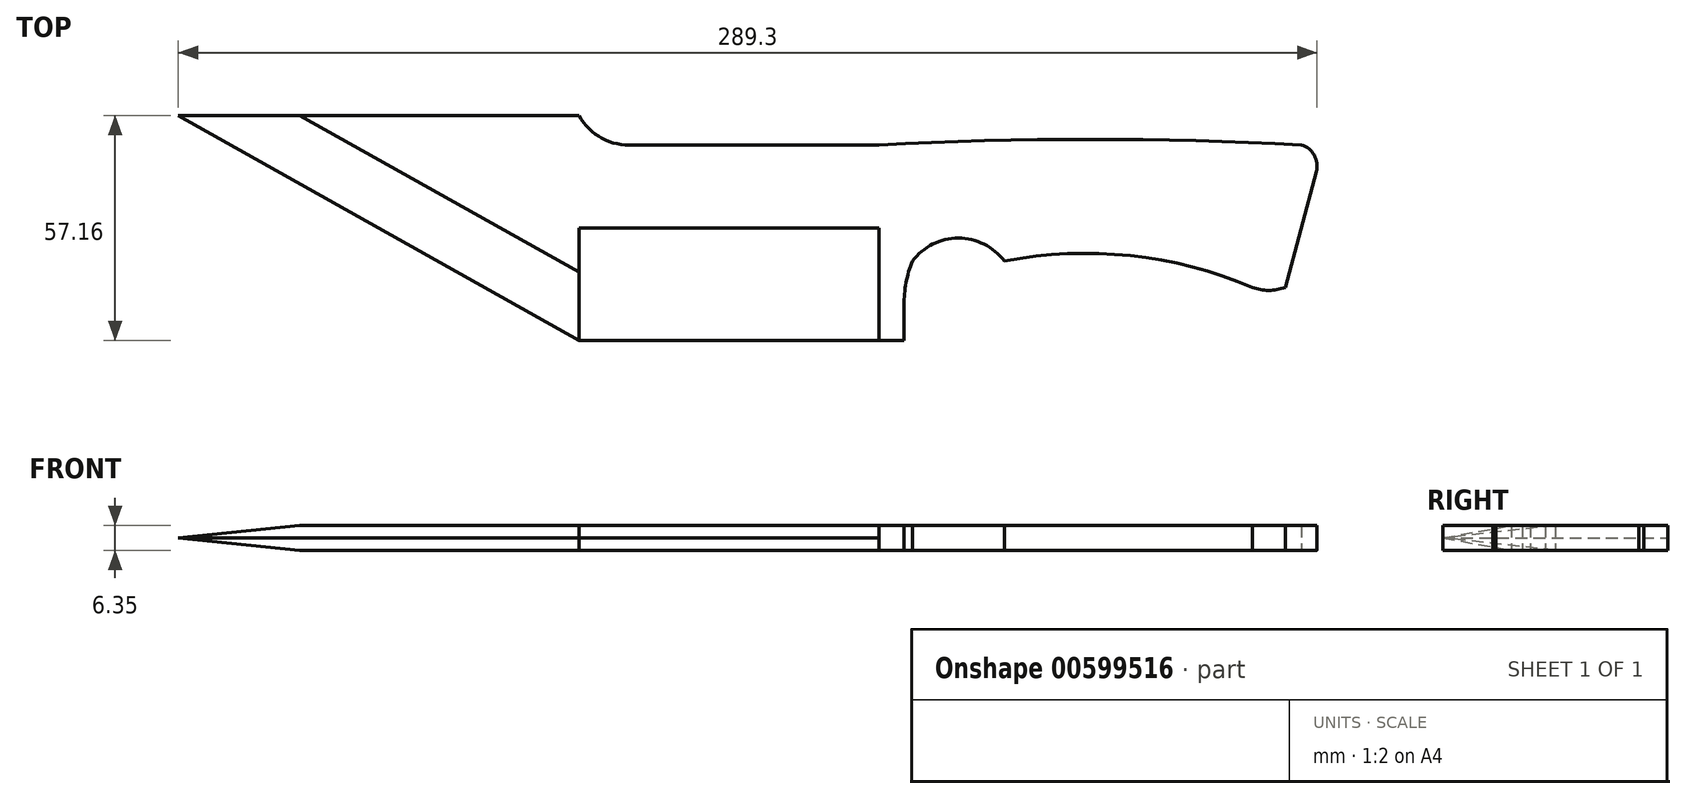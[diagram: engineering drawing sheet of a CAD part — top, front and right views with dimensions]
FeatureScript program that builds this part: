
annotation { "Feature Type Name" : "Feature", "Feature Type Description" : "" }
export const myFeature = defineFeature(function(context is Context, id is Id, definition is map)
    precondition{}
    {
        {
            var Q0;
            Q0=qCreatedBy(makeId("Top.planeOp"),FACE);
            var sketch = newSketch(context, id + "F0", { "sketchPlane" : qUnion([Q0])});
            skPoint(sketch, "E0.middle", {"position": v(0, 0) * mm});
            skLineSegment(sketch, "E1", {"start": v(-44.2, -28.58) * mm, "end": v(-146.05, 28.58) * mm});
            skLineSegment(sketch, "E2", {"start": v(-44.2, -28.58) * mm, "end": v(31.94, -28.58) * mm});
            skLineSegment(sketch, "E3", {"start": v(31.94, -28.58) * mm, "end": v(38.32, -28.58) * mm});
            skArc(sketch, "E4", {"start": v(-44.2, 28.58) * mm, "mid": v(-38.45, 22.79) * mm, "end": v(-30.46, 21.12) * mm});
            skLineSegment(sketch, "E5", {"start": v(-30.46, 21.12) * mm, "end": v(31.94, 21.12) * mm});
            skLineSegment(sketch, "E6", {"start": v(-146.05, 28.58) * mm, "end": v(-44.2, 28.58) * mm});
            skLineSegment(sketch, "E7", {"start": v(38.32, -28.58) * mm, "end": v(38.32, -19.6) * mm});
            skArc(sketch, "E8", {"start": v(139.27, 21.12) * mm, "mid": v(85.6, 22.5) * mm, "end": v(31.94, 21.12) * mm});
            skArc(sketch, "E9", {"start": v(143.06, 14.34) * mm, "mid": v(142.54, 18.5) * mm, "end": v(139.27, 21.12) * mm});
            skLineSegment(sketch, "E10", {"start": v(143.06, 14.34) * mm, "end": v(135.17, -15.1) * mm});
            skArc(sketch, "E11", {"start": v(126.78, -15.1) * mm, "mid": v(130.97, -15.85) * mm, "end": v(135.17, -15.1) * mm});
            skArc(sketch, "E12", {"start": v(126.78, -15.1) * mm, "mid": v(95.81, -7.04) * mm, "end": v(63.84, -8.4) * mm});
            skArc(sketch, "E13", {"start": v(63.84, -8.4) * mm, "mid": v(52.15, -2.59) * mm, "end": v(40.45, -8.4) * mm});
            skArc(sketch, "E14", {"start": v(40.45, -8.4) * mm, "mid": v(38.86, -13.9) * mm, "end": v(38.32, -19.6) * mm});
            skLineSegment(sketch, "E15", {"start": v(31.94, -10.1) * mm, "end": v(31.94, -28.58) * mm});
            skLineSegment(sketch, "E16", {"start": v(-115.17, 28.58) * mm, "end": v(-44.2, -11.25) * mm});
            skLineSegment(sketch, "E17", {"start": v(-44.2, 0) * mm, "end": v(31.94, 0) * mm});
            skLineSegment(sketch, "E18", {"start": v(31.94, 0) * mm, "end": v(31.94, -10.1) * mm});
            skLineSegment(sketch, "E19", {"start": v(-44.2, 0) * mm, "end": v(-44.2, -28.58) * mm});
            skSolve(sketch);
        }
        {
            var Q0;
            Q0=makeQuery(id+"F0.imprint","IMPRINT",FACE,{"disambiguationData":[TD([[makeQuery(id+"F0.imprint","IMPRINT",EDGE,{"derivedFrom":sQuery(id+"F0.wireOp",EDGE,"E3")}),1.0]])]});
            extrude(context, id + "F1", {"entities" : qUnion([Q0]), "depth" : 6.35 * mm, "offsetDistance" : 25.4 * mm});
        }
        {
            var Q0;
            {var subQ5=sQuery(id+"F0.wireOp",EDGE,"E1");Q0=makeQuery(id+"F0.imprint","IMPRINT",FACE,{"disambiguationData":[TD([[makeQuery(id+"F0.imprint","IMPRINT",EDGE,{"derivedFrom":subQ5}),-1.0]])]});}
            extrude(context, id + "F2", {"entities" : qUnion([Q0]), "depth" : 6.35 * mm, "offsetDistance" : 25.4 * mm});
        }
        {
            var Q0;
            Q0=makeQuery(id+"F2.opExtrude","CAP_EDGE",EDGE,{"disambiguationData":[OSD([sQuery(id+"F0.wireOp",EDGE,"E1")])],"isStart":false});
            var Q1;
            Q1=makeQuery(id+"F2.opExtrude","CAP_EDGE",EDGE,{"disambiguationData":[OSD([sQuery(id+"F0.wireOp",EDGE,"E1")])],"isStart":true});
            chamfer(context, id + "F3", {"entities" : qUnion([Q0, Q1]), "chamferType" : ChamferType.TWO_OFFSETS, "width1" : 3.17 * mm, "oppositeDirection" : false, "width2" : 15.24 * mm, "tangentPropagation" : true});
        }
        {
            var Q0;
            {var subQ1=sQuery(id+"F0.wireOp",EDGE,"E2");Q0=makeQuery(id+"F0.imprint","IMPRINT",FACE,{"disambiguationData":[TD([[makeQuery(id+"F0.imprint","IMPRINT",EDGE,{"derivedFrom":subQ1}),1.0]])]});}
            extrude(context, id + "F4", {"entities" : qUnion([Q0]), "depth" : 6.35 * mm, "offsetDistance" : 25.4 * mm});
        }
        {
            var Q0;
            Q0=makeQuery(id+"F4.opExtrude","CAP_EDGE",EDGE,{"disambiguationData":[OSD([sQuery(id+"F0.wireOp",EDGE,"E2")])],"isStart":false});
            var Q1;
            Q1=makeQuery(id+"F4.opExtrude","CAP_EDGE",EDGE,{"disambiguationData":[OSD([sQuery(id+"F0.wireOp",EDGE,"E2")])],"isStart":true});
            chamfer(context, id + "F5", {"entities" : qUnion([Q0, Q1]), "chamferType" : ChamferType.TWO_OFFSETS, "width1" : 28.57 * mm, "oppositeDirection" : false, "width2" : 3.17 * mm, "tangentPropagation" : true});
        }
    });
